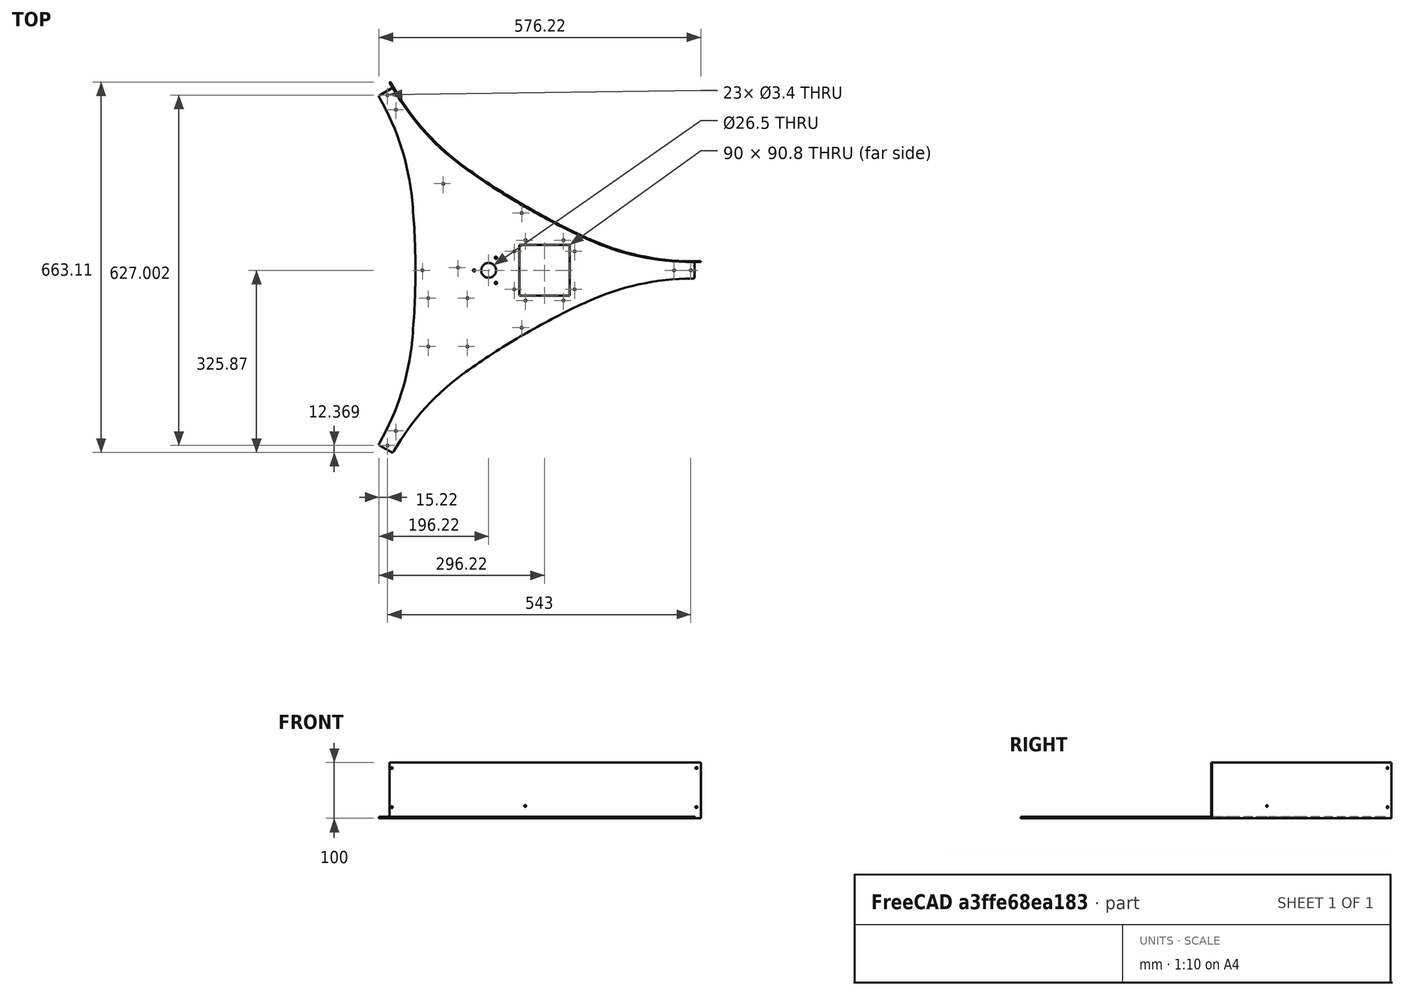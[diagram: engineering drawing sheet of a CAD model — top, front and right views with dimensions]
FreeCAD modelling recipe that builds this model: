
FCSTD DOCUMENT  (FreeCAD 1.1R38827 (Git))
Label: composit_stand3_hat_bottom_main
License: All rights reserved
LicenseURL: http://en.wikipedia.org/wiki/All_rights_reserved
objects: Part::FeaturePython×3, Part::Feature×2, Sketcher::SketchObject×2
note: 9 computed .brp shape members not serialized (recipe doc carries the construction recipe); baked Part::Feature solids carry a one-line shape summary decoded from their .brp
EXTERNAL_REF file=composit_stand3_basement_bottom_main.FCStd obj=Placment

FEATURE [Part::FeaturePython] Placment  label="pcb_placement"  # WARN: FeaturePython — macro-defined, semantics opaque (R4)
  AttacherType = Attacher::AttachEngine3D
  ExposePlacement = true
  MarkerShape = 1
  MarkerSize = 20
  NumElements = 1
  Placement = pos=(-30,-50,0) rot=(0,0,1;1.5708rad)
  Type = lattice2AttachablePlacement.AttachablePlacement
  isLattice = 1
FEATURE [Part::FeaturePython] Placment001  label="pu_placement"  # WARN: FeaturePython — macro-defined, semantics opaque (R4)
  AttacherType = Attacher::AttachEngine3D
  ExposePlacement = true
  MarkerShape = 1
  MarkerSize = 20
  NumElements = 1
  Placement = pos=(-30,30,0) rot=(0,0,1;1.5708rad)
  Type = lattice2AttachablePlacement.AttachablePlacement
  isLattice = 1
FEATURE [Part::FeaturePython] Placment002  label="filter_placement"  # WARN: FeaturePython — macro-defined, semantics opaque (R4)
  AttacherType = Attacher::AttachEngine3D
  ExposePlacement = true
  MarkerShape = 1
  MarkerSize = 20
  NumElements = 1
  Placement = pos=(40,0,0) rot=(0,0,1;0rad)
  Type = lattice2AttachablePlacement.AttachablePlacement
  isLattice = 1
FEATURE [Part::Feature] Body172  label="hat3_plexiglass001"
  Placement = pos=(0,0,0) rot=(0,0,1;0.523599rad)
  shape: bbox 557.2 x 322.4 x 100 mm, 43 faces (baked)
FEATURE [Sketcher::SketchObject] Sketch001
  ArcFitTolerance = 1e-06
  FullyConstrained = false
  MakeInternals = false
  expr: Constraints[12] = <<composit_stand3_basement_bottom_main>>#<<bar_placement>>.Placement.Base.x - 14.5 mm
  sketch-geometry (5):
    g0: LineSegment StartX=61.9366 StartY=97.2774 StartZ=0 EndX=57.6065 EndY=99.7774 EndZ=0
    g1: ArcOfCircle CenterX=369 CenterY=629.127 CenterZ=0 NormalX=0 NormalY=0 NormalZ=1 AngleXU=0 Radius=614.127 StartAngle=4.18879 EndAngle=4.71239
    g2: GeomPoint [constr] X=202.184 Y=16.3053 Z=0
    g3: LineSegment [constr] StartX=0 StartY=0 StartZ=0 EndX=57.6065 EndY=99.7774 EndZ=0
    g4: LineSegment [constr] StartX=369 StartY=15 StartZ=0 EndX=369 EndY=0 EndZ=0
  constraints (14):
    c: PointOnObject(g2,g0)
    c: Tangent(g0,g1) = 1.5708
    c: Coincident(g3,g-1)
    c: Coincident(g3,g0)
    c: Angle(g3) = 1.0472
    c: Perpendicular(g3,g0)
    c: Distance(g0) = 5
    c: Radius(g1) = 614.127  'r'
    c: Coincident(g4,g1)
    c: PointOnObject(g4,g-1)
    c: Vertical(g4)
    c: Perpendicular(g1,g4)
    c: DistanceX(g1) = 369
    c: DistanceY(g1) = 15
FEATURE [Sketcher::SketchObject] Sketch  label="main_sketch"
  ArcFitTolerance = 0
  ExternalGeometry = -> [Sketch001]
  FullyConstrained = true
  MakeInternals = false
  sketch-geometry (6):
    g0: LineSegment StartX=369 StartY=0 StartZ=0 EndX=369 EndY=13.0033 EndZ=0
    g1: ArcOfCircle CenterX=367 CenterY=13.0033 CenterZ=0 NormalX=0 NormalY=0 NormalZ=1 AngleXU=0 Radius=2 StartAngle=2e-16 EndAngle=1.5708
    g2: LineSegment [constr] StartX=0 StartY=15.0033 StartZ=0 EndX=367 EndY=15.0033 EndZ=0
    g3: GeomPoint [constr] X=369 Y=15.0033 Z=0
    g4: ArcOfCircle CenterX=367 CenterY=621.711 CenterZ=0 NormalX=0 NormalY=0 NormalZ=1 AngleXU=0 Radius=606.708 StartAngle=4.18553 EndAngle=4.71239
    g5: LineSegment StartX=57.6065 StartY=99.7774 StartZ=0 EndX=61.9366 EndY=97.2774 EndZ=0
  constraints (16):
    c: PointOnObject(g0,g-1)
    c: Vertical(g0)
    c: Tangent(g4,g1) = 1.5708
    c: Tangent(g1,g0) = -1.5708
    c: Radius(g1) = 2
    c: PointOnObject(g2,g-2)
    c: Horizontal(g2)
    c: Tangent(g2,g1) = 1.5708
    c: PointOnObject(g3,g2)
    c: PointOnObject(g3,g0)
    c: Tangent(g4,g2)
    c: Coincident(g4,g-4)
    c: Coincident(g5,g4)
    c: PointOnObject(g1,g-3)
    c: Vertical(g0,g-3)
    c: Coincident(g5,g-4)
FEATURE [Part::Feature] Body173  label="hat3_base001"
  Placement = pos=(0,0,0) rot=(0,0,1;-1.5708rad)
  shape: bbox 565.2 x 651.7 x 3 mm, 69 faces (baked)
